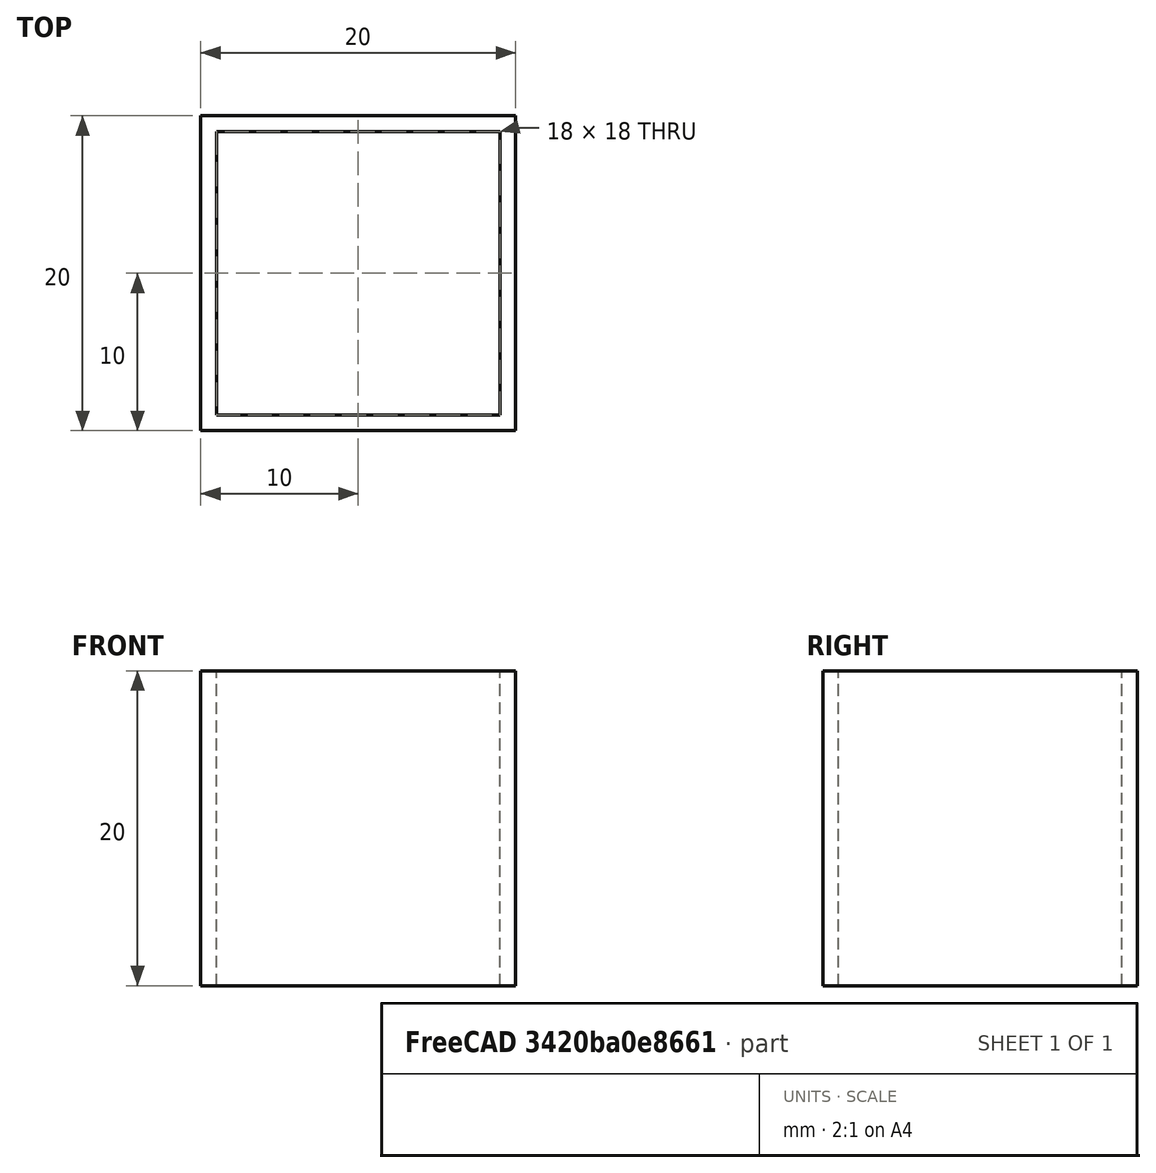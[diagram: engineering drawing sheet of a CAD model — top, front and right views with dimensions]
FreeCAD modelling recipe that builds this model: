
FCSTD DOCUMENT  (FreeCAD 2023.1018R14555 (Git shallow))
Label: wall-width-test
License: All rights reserved
LicenseURL: https://en.wikipedia.org/wiki/All_rights_reserved
objects: Sketcher::SketchObject×1, PartDesign::Pad×1, PartDesign::Body×1
note: 6 computed .brp shape members not serialized (recipe doc carries the construction recipe); baked Part::Feature solids carry a one-line shape summary decoded from their .brp

FEATURE [Sketcher::SketchObject] Sketch
  ArcFitTolerance = 1e-06
  AttachmentSupport = -> [XY_Plane]
  ExternalBSplineMaxDegree = 5
  ExternalBSplineTolerance = 0.0001
  FullyConstrained = true
  InternalTolerance = 1e-06
  InvalidShape = false
  MakeInternals = false
  MapMode = 5
  Support = -> [XY_Plane]
  TreeRank = 13
  ValidateShape = false
  sketch-geometry (12):
    g0: LineSegment StartX=-9 StartY=-9 StartZ=0 EndX=-9 EndY=9 EndZ=0
    g1: LineSegment StartX=-9 StartY=9 StartZ=0 EndX=9 EndY=9 EndZ=0
    g2: LineSegment StartX=9 StartY=9 StartZ=0 EndX=9 EndY=-9 EndZ=0
    g3: LineSegment StartX=9 StartY=-9 StartZ=0 EndX=-9 EndY=-9 EndZ=0
    g4: GeomPoint [constr] X=0 Y=0 Z=0
    g5: LineSegment StartX=-10 StartY=-10 StartZ=0 EndX=-10 EndY=10 EndZ=0
    g6: LineSegment StartX=-10 StartY=10 StartZ=0 EndX=10 EndY=10 EndZ=0
    g7: LineSegment StartX=10 StartY=10 StartZ=0 EndX=10 EndY=-10 EndZ=0
    g8: LineSegment StartX=10 StartY=-10 StartZ=0 EndX=-10 EndY=-10 EndZ=0
    g9: GeomPoint [constr] X=0 Y=0 Z=0
    g10: LineSegment [constr] StartX=9 StartY=9 StartZ=0 EndX=10 EndY=9 EndZ=0
    g11: LineSegment [constr] StartX=9 StartY=9 StartZ=0 EndX=9 EndY=10 EndZ=0
  constraints (30):
    c: Coincident(g0,g1)
    c: Coincident(g1,g2)
    c: Coincident(g2,g3)
    c: Coincident(g3,g0)
    c: Horizontal(g1)
    c: Horizontal(g3)
    c: Vertical(g0)
    c: Vertical(g2)
    c: Symmetric(g1,g0,g4)
    c: Coincident(g4,g-1)
    c: Coincident(g5,g6)
    c: Coincident(g6,g7)
    c: Coincident(g7,g8)
    c: Coincident(g8,g5)
    c: Horizontal(g6)
    c: Horizontal(g8)
    c: Vertical(g5)
    c: Vertical(g7)
    c: Symmetric(g6,g5,g9)
    c: Coincident(g9,g4)
    c: Coincident(g10,g1)
    c: PointOnObject(g10,g7)
    c: Horizontal(g10)
    c: Coincident(g11,g1)
    c: PointOnObject(g11,g6)
    c: Vertical(g11)
    c: Equal(g11,g10)
    c: DistanceY(g11,g11) = 1
    c: DistanceY(g7,g7) = 20
    c: Equal(g7,g6)
FEATURE [PartDesign::Pad] Pad
  AddSubType = 0
  AlongSketchNormal = false
  AutoTaperInnerAngle = true
  CheckUpToFaceLimits = true
  ClaimChildren = false
  Direction = (0,0,1)
  Fit = 0
  FitJoin = 0
  InnerFit = 0
  InnerFitJoin = 0
  InvalidShape = false
  Length = 20
  Length2 = 10
  Linearize = true
  NewSolid = false
  Profile = -> Sketch
  ReferenceAxis = -> Sketch [N_Axis]
  Suppress = false
  TaperInnerAngle = 0
  TaperInnerAngleRev = 0
  TreeRank = 14
  Type = 0
  ValidateShape = true
  _ProfileBasedVersion = 1
FEATURE [PartDesign::Body] Body  label="wall-width-test-1mm"
  AutoGroupSolids = false
  ClaimAllChildren = false
  ExportMode = 0
  Group = -> [Sketch,Pad]
  InvalidShape = false
  Origin = -> Origin
  Tip = -> Pad
  TreeRank = 12
  ValidateShape = false
  _ExportChildren = -> [Pad]
  _GroupVersion = 1
